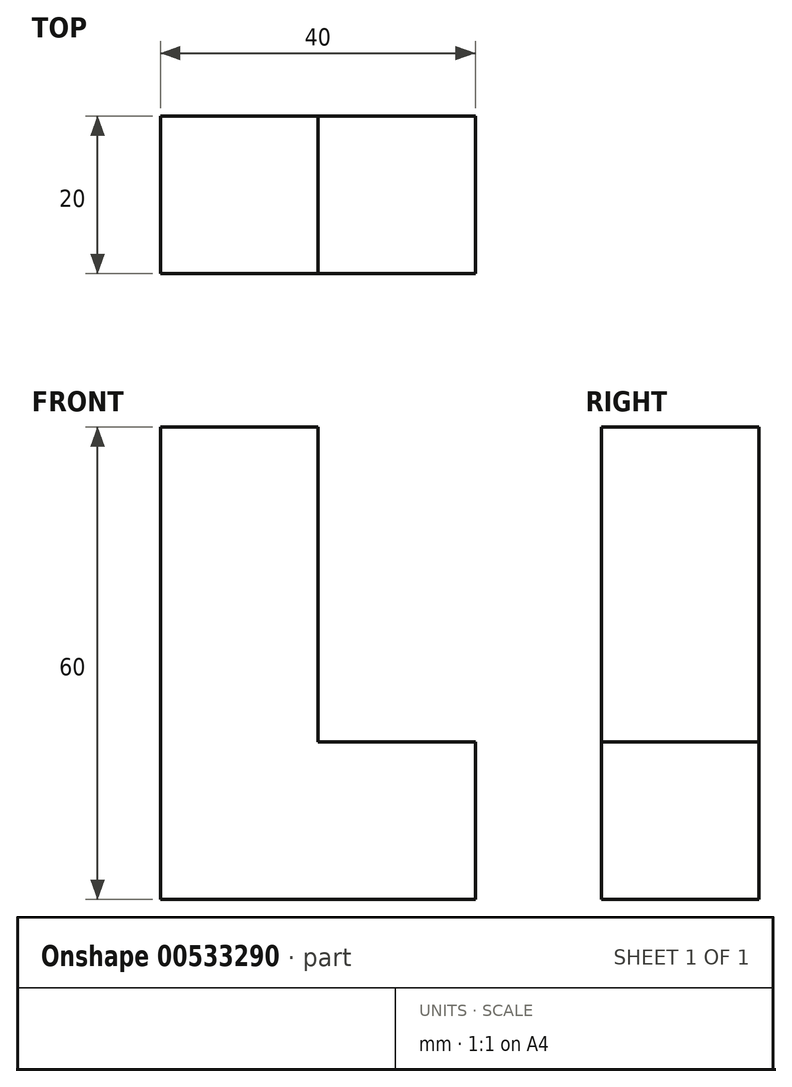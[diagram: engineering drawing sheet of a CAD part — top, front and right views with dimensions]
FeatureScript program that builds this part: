
annotation { "Feature Type Name" : "Feature", "Feature Type Description" : "" }
export const myFeature = defineFeature(function(context is Context, id is Id, definition is map)
    precondition{}
    {
        {
            var Q0;
            Q0=qCreatedBy(makeId("Front.planeOp"),FACE);
            var sketch = newSketch(context, id + "F0", { "sketchPlane" : qUnion([Q0])});
            skLineSegment(sketch, "E0", {"start": v(-44.52, 38.78) * mm, "end": v(-24.52, 38.78) * mm});
            skLineSegment(sketch, "E1", {"start": v(-24.52, -1.22) * mm, "end": v(-4.52, -1.22) * mm});
            skLineSegment(sketch, "E2", {"start": v(-4.52, -1.22) * mm, "end": v(-4.52, -21.22) * mm});
            skLineSegment(sketch, "E3", {"start": v(-4.52, -21.22) * mm, "end": v(-44.52, -21.22) * mm});
            skLineSegment(sketch, "E4", {"start": v(-44.52, -21.22) * mm, "end": v(-44.52, 38.78) * mm});
            skLineSegment(sketch, "E5", {"start": v(-24.52, 38.78) * mm, "end": v(-24.52, -1.22) * mm});
            skSolve(sketch);
        }
        {
            var Q0;
            Q0 = qSketchRegion(id + "F0", true);
            extrude(context, id + "F1", {"entities" : qUnion([Q0]), "depth" : 20 * mm, "offsetDistance" : 25 * mm});
        }
    });
